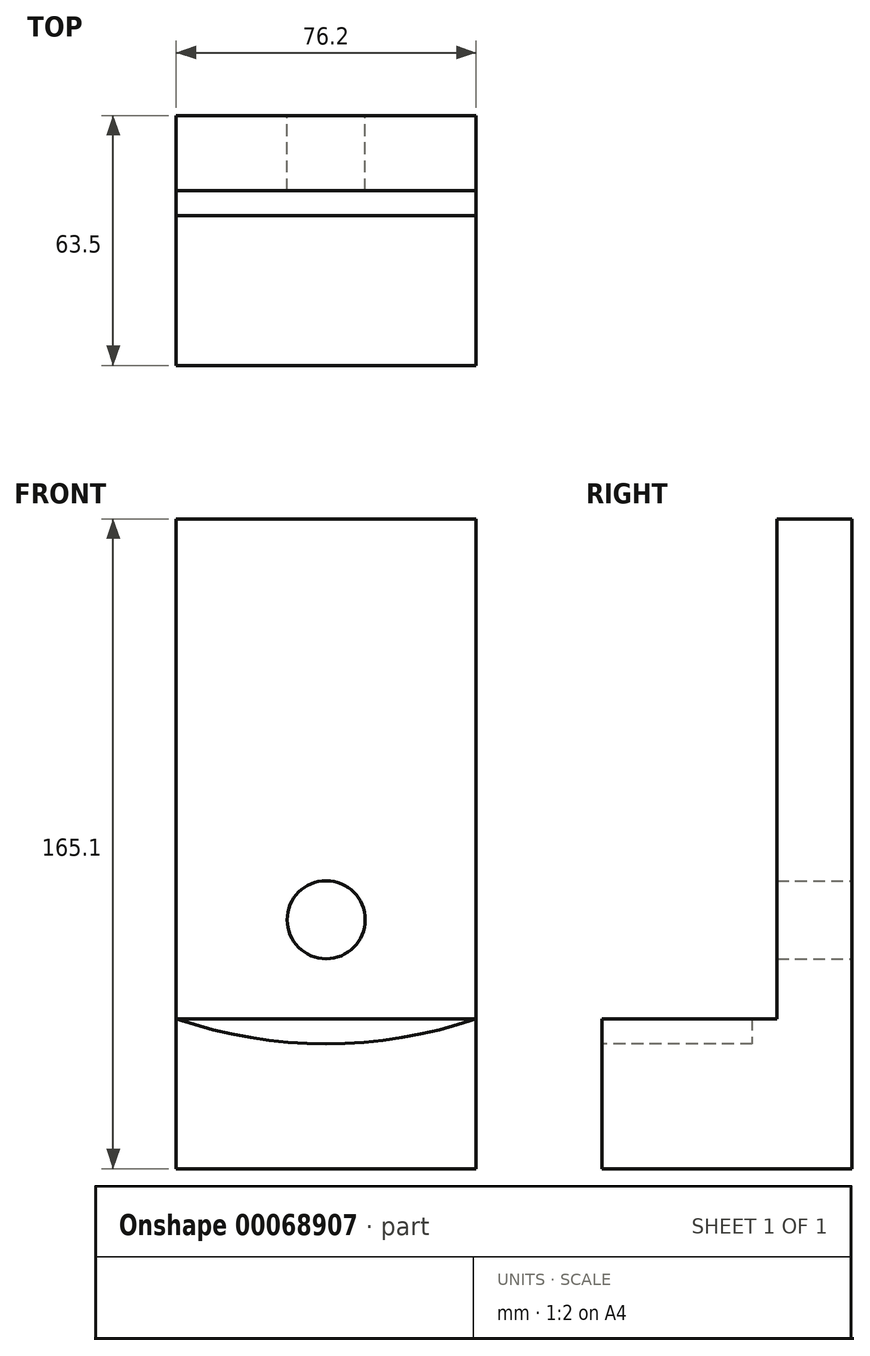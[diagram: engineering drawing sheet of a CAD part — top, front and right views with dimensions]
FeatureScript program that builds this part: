
annotation { "Feature Type Name" : "Feature", "Feature Type Description" : "" }
export const myFeature = defineFeature(function(context is Context, id is Id, definition is map)
    precondition{}
    {
        {
            var Q0;
            Q0=qCreatedBy(makeId("Top.planeOp"),FACE);
            var sketch = newSketch(context, id + "F0", { "sketchPlane" : qUnion([Q0])});
            skLineSegment(sketch, "E0.rect.bottom", {"start": v(-38.1, 31.75) * mm, "end": v(38.1, 31.75) * mm});
            skLineSegment(sketch, "E0.rect.top", {"start": v(-38.1, -31.75) * mm, "end": v(38.1, -31.75) * mm});
            skLineSegment(sketch, "E0.rect.left", {"start": v(-38.1, 31.75) * mm, "end": v(-38.1, -31.75) * mm});
            skLineSegment(sketch, "E0.rect.right", {"start": v(38.1, 31.75) * mm, "end": v(38.1, -31.75) * mm});
            skPoint(sketch, "E0.rect.middle", {"position": v(0, 0) * mm});
            skLineSegment(sketch, "E1", {"start": v(38.1, -31.75) * mm, "end": v(-38.1, 31.75) * mm, "construction": true});
            skSolve(sketch);
        }
        {
            var Q0;
            Q0 = qSketchRegion(id + "F0", true);
            extrude(context, id + "F1", {"entities" : qUnion([Q0]), "depth" : 38.1 * mm});
        }
        {
            var Q0;
            Q0=makeQuery(id+"F1.opExtrude","CAP_FACE",FACE,{"disambiguationData":[OSD([sQuery(id+"F0.wireOp",EDGE,"E0.rect.bottom"),sQuery(id+"F0.wireOp",EDGE,"E0.rect.top"),sQuery(id+"F0.wireOp",EDGE,"E0.rect.left"),sQuery(id+"F0.wireOp",EDGE,"E0.rect.right")])],"isStart":false});
            var sketch = newSketch(context, id + "F2", { "sketchPlane" : qUnion([Q0])});
            skLineSegment(sketch, "E2.0", {"start": v(-38.1, 31.75) * mm, "end": v(38.1, 31.75) * mm});
            skLineSegment(sketch, "E3", {"start": v(38.1, 12.7) * mm, "end": v(38.1, 31.75) * mm});
            skLineSegment(sketch, "E4", {"start": v(-38.1, 12.7) * mm, "end": v(38.1, 12.7) * mm});
            skLineSegment(sketch, "E5", {"start": v(-38.1, 12.7) * mm, "end": v(-38.1, 31.75) * mm});
            skSolve(sketch);
        }
        {
            var Q0;
            Q0 = qSketchRegion(id + "F2", true);
            extrude(context, id + "F7", {"entities" : qUnion([Q0]), "operationType" : NewBodyOperationType.ADD, "depth" : 127 * mm});
        }
        {
            var Q0;
            Q0=makeQuery(id+"F7.boolean.opBoolean","MERGE",FACE,{"derivedFrom":[makeQuery(id+"F1.opExtrude","SWEPT_FACE",FACE,{"disambiguationData":[OSD([sQuery(id+"F0.wireOp",EDGE,"E0.rect.bottom")])]}),makeQuery(id+"F7.opExtrude","SWEPT_FACE",FACE,{"disambiguationData":[OSD([sQuery(id+"F2.wireOp",EDGE,"E2.0")])]})]});
            var sketch = newSketch(context, id + "F3", { "sketchPlane" : qUnion([Q0])});
            skPoint(sketch, "E6", {"position": v(0, 63.23) * mm});
            skLineSegment(sketch, "E7", {"start": v(0, 165.1) * mm, "end": v(0, -0.27) * mm, "construction": true});
            skSolve(sketch);
        }
        {
            var Q0;
            Q0=sQuery(id+"F3.wireOp",VERTEX,"E6");
            var Q1;
            Q1=makeQuery(id+"F1.opExtrude","SWEPT_BODY",BODY,{"disambiguationData":[OSD([sQuery(id+"F0.wireOp",EDGE,"E0.rect.bottom"),sQuery(id+"F0.wireOp",EDGE,"E0.rect.top"),sQuery(id+"F0.wireOp",EDGE,"E0.rect.left"),sQuery(id+"F0.wireOp",EDGE,"E0.rect.right")])]});
            hole(context, id + "F4", {"style" : HoleStyle.SIMPLE, "holeDiameter" : 19.84 * mm, "endStyle" : HoleEndStyle.THROUGH, "locations" : qUnion([Q0]), "scope" : qUnion([Q1]), "standardTappedOrClearance" : lookupTablePath({ "fit" : "Normal (ASME)", "standard" : "ANSI", "size" : "3/4", "type" : "Clearance" }), "standardBlindInLast" : lookupTablePath({ "fit" : "Free", "standard" : "ANSI", "size" : "3/4", "type" : "Clearance" }), "tappedDepth" : 12.7 * mm, "tapClearance" : 3});
        }
        {
            var Q0;
            Q0=makeQuery(id+"F1.opExtrude","SWEPT_FACE",FACE,{"disambiguationData":[OSD([sQuery(id+"F0.wireOp",EDGE,"E0.rect.top")])]});
            var sketch = newSketch(context, id + "F5", { "sketchPlane" : qUnion([Q0])});
            skArc(sketch, "E8", {"start": v(-38.1, 38.1) * mm, "mid": v(0, 31.73) * mm, "end": v(38.1, 38.1) * mm});
            skLineSegment(sketch, "E9.0", {"start": v(-38.1, 38.1) * mm, "end": v(38.1, 38.1) * mm});
            skSolve(sketch);
        }
        {
            var Q0;
            Q0 = qSketchRegion(id + "F5", true);
            var Q1;
            Q1=makeQuery(id+"F7.opExtrude","SWEPT_FACE",FACE,{"disambiguationData":[OSD([sQuery(id+"F2.wireOp",EDGE,"E4")])]});
            extrude(context, id + "F6", {"entities" : qUnion([Q0]), "operationType" : NewBodyOperationType.REMOVE, "endBound" : BoundingType.UP_TO_NEXT, "oppositeDirection" : true, "depth" : 25.4 * mm, "endBoundEntityFace" : qUnion([Q1]), "hasOffset" : true, "offsetDistance" : 25.4 * mm});
        }
    });
